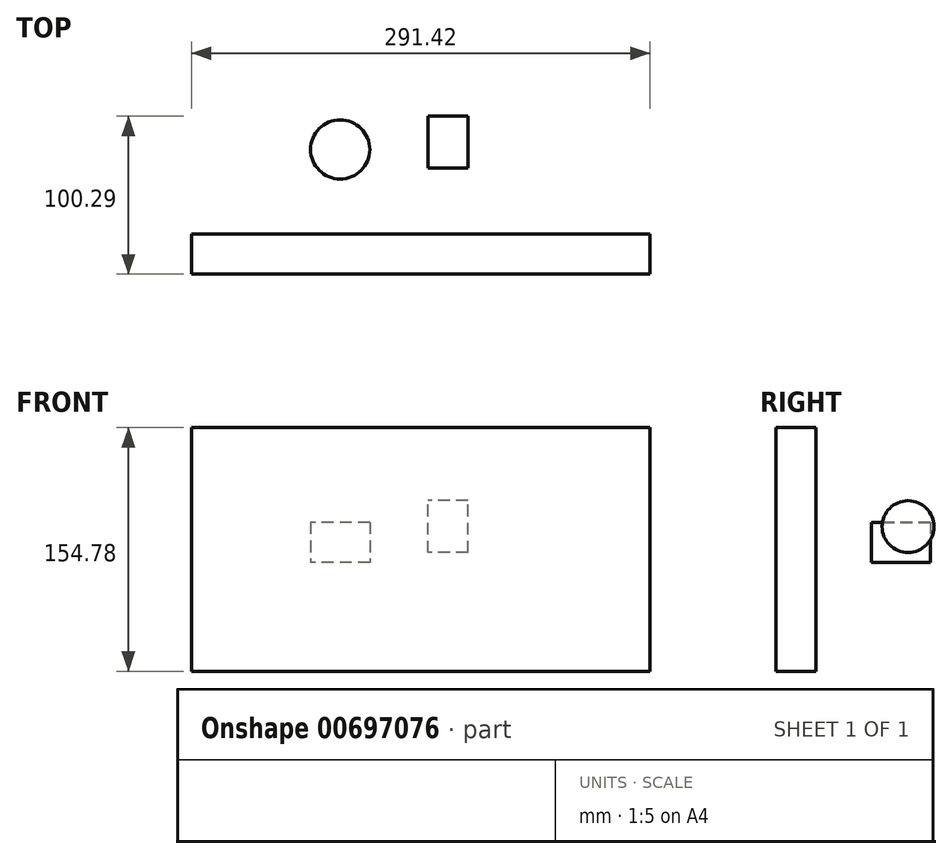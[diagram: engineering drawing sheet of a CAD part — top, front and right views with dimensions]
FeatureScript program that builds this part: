
annotation { "Feature Type Name" : "Feature", "Feature Type Description" : "" }
export const myFeature = defineFeature(function(context is Context, id is Id, definition is map)
    precondition{}
    {
        {
            var Q0;
            Q0=qCreatedBy(makeId("Front.planeOp"),FACE);
            var sketch = newSketch(context, id + "F0", { "sketchPlane" : qUnion([Q0])});
            skLineSegment(sketch, "E0.bottom", {"start": v(-150.33, 85.58) * mm, "end": v(141.1, 85.58) * mm});
            skLineSegment(sketch, "E0.top", {"start": v(-150.33, -69.2) * mm, "end": v(141.1, -69.2) * mm});
            skLineSegment(sketch, "E0.left", {"start": v(-150.33, 85.58) * mm, "end": v(-150.33, -69.2) * mm});
            skLineSegment(sketch, "E0.right", {"start": v(141.1, 85.58) * mm, "end": v(141.1, -69.2) * mm});
            skSolve(sketch);
        }
        {
            var Q0;
            Q0=makeQuery(id+"F0.imprint","IMPRINT",FACE,{"disambiguationData":[TD([[makeQuery(id+"F0.imprint","IMPRINT",EDGE,{"derivedFrom":sQuery(id+"F0.wireOp",EDGE,"E0.bottom")}),-1.0]])]});
            extrude(context, id + "F1", {"entities" : qUnion([Q0]), "depth" : 25.4 * mm, "offsetDistance" : 25.4 * mm});
        }
        {
            var Q0;
            Q0=qCreatedBy(makeId("Right.planeOp"),FACE);
            var sketch = newSketch(context, id + "F2", { "sketchPlane" : qUnion([Q0])});
            skCircle(sketch, "E1", {"center": v(58.4, 22.67) * mm, "radius": 16.5 * mm});
            skSolve(sketch);
        }
        {
            var Q0;
            Q0 = qSketchRegion(id + "F2", true);
            extrude(context, id + "F3", {"entities" : qUnion([Q0]), "depth" : 25.4 * mm, "offsetDistance" : 25.4 * mm});
        }
        {
            var Q0;
            Q0=qCreatedBy(makeId("Top.planeOp"),FACE);
            var sketch = newSketch(context, id + "F4", { "sketchPlane" : qUnion([Q0])});
            skCircle(sketch, "E2", {"center": v(-55.8, 53.79) * mm, "radius": 18.8 * mm});
            skSolve(sketch);
        }
        {
            var Q0;
            Q0 = qSketchRegion(id + "F4", true);
            extrude(context, id + "F5", {"entities" : qUnion([Q0]), "depth" : 25.4 * mm, "offsetDistance" : 25.4 * mm});
        }
    });
